# Revit family: Estacion Mantenimiento Biki
name_source: partatom
category: Furniture
units: mm (PartAtom-declared; Revit-internal decimal feet)

## family parameters
Always vertical = Yes
Cut with Voids When Loaded = No
Room Calculation Point = No
Shared = No
Work Plane-Based = No

## types (1)
- Estación Mantenimiento Biki-VBE01-1500mm
    A = 0.22 m
    Default Elevation = 0 m
    Description = La estación incluye varias herramientas como una bomba de pie de aire para inflar las ruedas, llaves hexagonales allen de diferentes tamaños,
llave inglesa, alicates, destornillador plano y de estrella y palancas para sacar la cubierta de la rueda.
    Ficha tecnica = https://www.benito.com
    H = 1.5 m
    Material = Acero con pintura
    Referencia = VBE01
    Type Comments = Fijación al suelo mediante 4 tornillos M8, no suministrados.
    URL Producto = https://www.benito.com

## geometry (parser evidence)
native form markers: Blend x6, Sweep x2
no freeform markers — native parametric forms only
